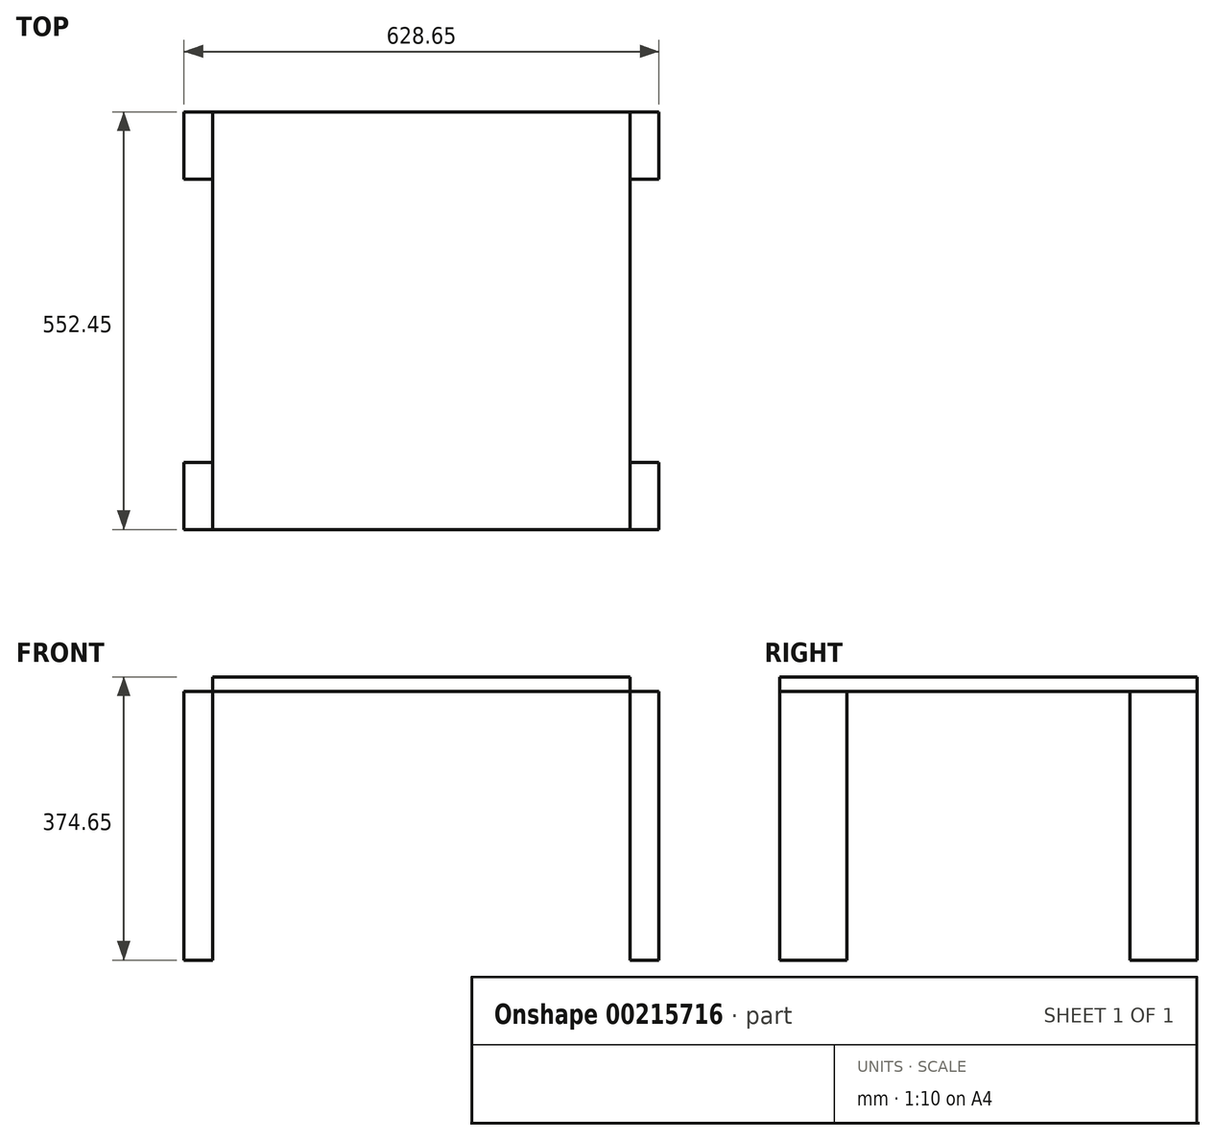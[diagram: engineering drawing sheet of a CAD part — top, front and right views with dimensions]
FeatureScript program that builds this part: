
annotation { "Feature Type Name" : "Feature", "Feature Type Description" : "" }
export const myFeature = defineFeature(function(context is Context, id is Id, definition is map)
    precondition{}
    {
        {
            var Q0;
            Q0=qCreatedBy(makeId("Top.planeOp"),FACE);
            var sketch = newSketch(context, id + "F0", { "sketchPlane" : qUnion([Q0])});
            skLineSegment(sketch, "E0.bottom", {"start": v(-252.42, 252.42) * mm, "end": v(300.03, 252.42) * mm});
            skLineSegment(sketch, "E0.top", {"start": v(-252.42, -300.03) * mm, "end": v(300.03, -300.03) * mm});
            skLineSegment(sketch, "E0.left", {"start": v(-252.42, 252.42) * mm, "end": v(-252.42, -300.03) * mm});
            skLineSegment(sketch, "E0.right", {"start": v(300.03, 252.42) * mm, "end": v(300.03, -300.03) * mm});
            skLineSegment(sketch, "E1", {"start": v(0, 252.42) * mm, "end": v(0, 0) * mm, "construction": true});
            skLineSegment(sketch, "E2", {"start": v(0, 0) * mm, "end": v(-252.42, 0) * mm, "construction": true});
            skSolve(sketch);
        }
        {
            var Q0;
            Q0 = qSketchRegion(id + "F0", true);
            extrude(context, id + "F1", {"entities" : qUnion([Q0]), "depth" : 19.05 * mm});
        }
        {
            var Q0;
            Q0=makeQuery(id+"F1.opExtrude","SWEPT_FACE",FACE,{"disambiguationData":[OSD([sQuery(id+"F0.wireOp",EDGE,"E0.right")])]});
            var sketch = newSketch(context, id + "F2", { "sketchPlane" : qUnion([Q0])});
            skLineSegment(sketch, "E3.bottom", {"start": v(-300.03, 0) * mm, "end": v(-211.13, 0) * mm});
            skLineSegment(sketch, "E3.top", {"start": v(-300.03, -355.6) * mm, "end": v(-211.13, -355.6) * mm});
            skLineSegment(sketch, "E3.left", {"start": v(-300.03, 0) * mm, "end": v(-300.03, -355.6) * mm});
            skLineSegment(sketch, "E3.right", {"start": v(-211.13, 0) * mm, "end": v(-211.13, -355.6) * mm});
            skLineSegment(sketch, "E4.bottom", {"start": v(252.42, 0) * mm, "end": v(163.52, 0) * mm});
            skLineSegment(sketch, "E4.top", {"start": v(252.42, -355.6) * mm, "end": v(163.52, -355.6) * mm});
            skLineSegment(sketch, "E4.left", {"start": v(252.42, 0) * mm, "end": v(252.42, -355.6) * mm});
            skLineSegment(sketch, "E4.right", {"start": v(163.52, 0) * mm, "end": v(163.52, -355.6) * mm});
            skSolve(sketch);
        }
        {
            var Q0;
            Q0 = qSketchRegion(id + "F2", true);
            extrude(context, id + "F3", {"entities" : qUnion([Q0]), "depth" : 38.1 * mm});
        }
        {
            var Q0;
            Q0=makeQuery(id+"F1.opExtrude","SWEPT_FACE",FACE,{"disambiguationData":[OSD([sQuery(id+"F0.wireOp",EDGE,"E0.left")])]});
            var sketch = newSketch(context, id + "F4", { "sketchPlane" : qUnion([Q0])});
            skLineSegment(sketch, "E5.bottom", {"start": v(-252.42, 0) * mm, "end": v(-163.52, 0) * mm});
            skLineSegment(sketch, "E5.top", {"start": v(-252.42, -355.6) * mm, "end": v(-163.52, -355.6) * mm});
            skLineSegment(sketch, "E5.left", {"start": v(-252.42, 0) * mm, "end": v(-252.42, -355.6) * mm});
            skLineSegment(sketch, "E5.right", {"start": v(-163.52, 0) * mm, "end": v(-163.52, -355.6) * mm});
            skLineSegment(sketch, "E6.bottom", {"start": v(300.03, 0) * mm, "end": v(211.13, 0) * mm});
            skLineSegment(sketch, "E6.top", {"start": v(300.03, -355.6) * mm, "end": v(211.13, -355.6) * mm});
            skLineSegment(sketch, "E6.left", {"start": v(300.03, 0) * mm, "end": v(300.03, -355.6) * mm});
            skLineSegment(sketch, "E6.right", {"start": v(211.13, 0) * mm, "end": v(211.13, -355.6) * mm});
            skSolve(sketch);
        }
        {
            var Q0;
            Q0 = qSketchRegion(id + "F4", true);
            extrude(context, id + "F5", {"entities" : qUnion([Q0]), "depth" : 38.1 * mm});
        }
    });
